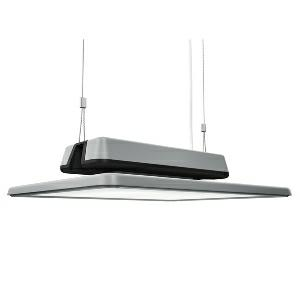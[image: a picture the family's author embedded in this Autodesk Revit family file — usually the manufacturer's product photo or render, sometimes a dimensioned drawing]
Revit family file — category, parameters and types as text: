
# Revit family: acaneo_-_hial_30000_840_w_dali_00733706_2762
name_source: partatom
category: Lighting Fixtures
units: mm (PartAtom-declared; Revit-internal decimal feet)

## family parameters
Cut with Voids When Loaded = No
Host = Face
Light Source = No
Part Type = Normal
Room Calculation Point = No
Round Connector Dimension = Use Diameter
Shared = No

## types (1)
- ACANEO - HIAL 30000/840/W/DALI (1 x LED, 33000 lm, 4000K)
    Apparent Load = 206 VA
    Approval mark = CE
    CIE Flux Codes = 76 97 99 100 100
    Color Rendering = 80-89
    Color Temperature = 4000K
    Control Gear = Electronic ballast
    Default Elevation = 1800 mm
    Description = HIAL 30000/840/W/DALI|High bay luminaire|light source: LED|work equipment: Adjustable electronic ballast, digital DALI|connected load: 220-240 V, 50/60 Hz|Power consumption: approx. 206 W|power factor: approx. 0,973|luminous flux: 33000 lm|luminous efficacy: 160 lm/W|colour temperature: Cold white, ca. 4000 K|color rendering index (CRI): >= 80|chromaticity tolerance:  3 SDCM|System of protection: IP 65|class of protection: I|technology: Continuously dimmable|luminaire body|material: Aluminium|surface: Powder coatet|colour: White aluminium|lamp cover: Acrylic (PMMA), Clear|weight (net): approx. 10.8 kg|mains lead: Built-in plug RST 20i5 Einbau|Fastening: Available separately|Accessory: Junction box (RST 20i5)|minimum ambient temperature: -30 ░C|maximum ambient temperature: 60 ░C|glare control: Optics|unified glare rating(4H 8H): <=  25|
    Frequency = 50 Hz, 60 Hz
    Height = 125 mm
    Lamp = 1 x LED
    Lamp Light Flux = 33000 lm
    Lamp count = 1
    Length = 585 mm
    Luminous efficacy = 160 lm/W
    Manufacturer = Waldmann
    ModVariant = No
    Model = 00733706
    Mounting Place = Ceiling
    Mounting Type = Pendant
    Number of Poles = 1
    OnlyDefault = Yes
    Power Factor = 1
    Product Name = ACANEO - HIAL 30000/840/W/DALI
    Product group = High bay luminaire (industry)
    ProductGroupID = 901
    Protection Class = Protection class I
    Protection Degree = IP 65
    RLX_Detail_Level = 1
    RLX_Emergency_Light_Flux = 0 lm
    RLX_Emergency_Type = 0
    RLX_Emergency_Type_DB = No
    RlxData = <blob elided: 29941 chars, md5=0a4e6c57>
    Socket = socket
    Standby Power = 0 W
    System Light Flux = 32999 lm
    System Power = 206 W
    Type Comments = Product without accessories
    Type Image = acaneo-hial.jpg
    URL = http://relux.com
    VarID = ---
    Voltage = 230 V
    Voltage Range = 110-120 V, 220-240 V
    Weight = 0.00 kg
    Width = 480 mm

## geometry (parser evidence)
native form markers: Blend x4, Sweep x9
no freeform markers — native parametric forms only
